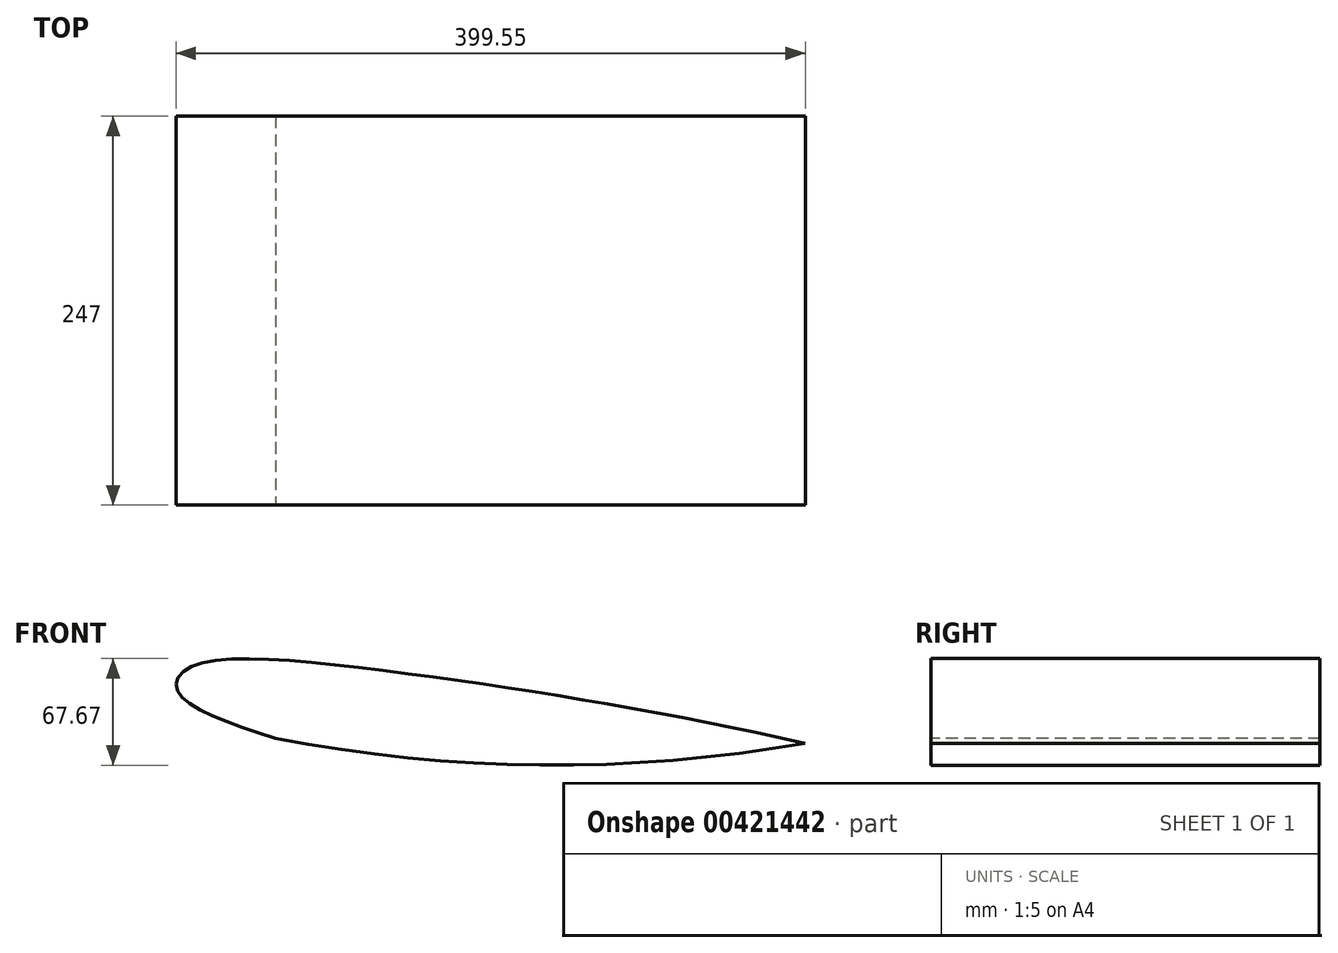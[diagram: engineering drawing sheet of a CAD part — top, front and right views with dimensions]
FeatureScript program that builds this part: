
annotation { "Feature Type Name" : "Feature", "Feature Type Description" : "" }
export const myFeature = defineFeature(function(context is Context, id is Id, definition is map)
    precondition{}
    {
        {
            var Q0;
            Q0=qCreatedBy(makeId("Front.planeOp"),FACE);
            var sketch = newSketch(context, id + "F0", { "sketchPlane" : qUnion([Q0])});
            skPoint(sketch, "E0", {"position": v(-1480.69, 132.06) * mm});
            skPoint(sketch, "E1", {"position": v(-1082.17, 99.2) * mm});
            skPoint(sketch, "E2", {"position": v(-1473.01, 147.53) * mm});
            skPoint(sketch, "E3", {"position": v(-1418.54, 102.28) * mm});
            skPoint(sketch, "E4", {"position": v(-1334.5, 143.28) * mm});
            skArc(sketch, "E5", {"start": v(-1418.54, 102.28) * mm, "mid": v(-1250.5, 85.26) * mm, "end": v(-1082.17, 99.2) * mm});
            skArc(sketch, "E6", {"start": v(-1334.5, 143.28) * mm, "mid": v(-1207.83, 124.11) * mm, "end": v(-1082.17, 99.2) * mm});
            skFitSpline(sketch, "E7", {"points": [v(-1418.54, 102.28) * mm, v(-1480.69, 132.06) * mm, v(-1473.01, 147.53) * mm, v(-1334.5, 143.28) * mm], "startDerivative": vector(-247.74, 81.4) * mm, "endDerivative": vector(361.63, -46.33) * mm});
            skSolve(sketch);
        }
        {
            var Q0;
            Q0=makeQuery(id+"F0.imprint","IMPRINT",FACE,{"disambiguationData":[TD([[makeQuery(id+"F0.imprint","IMPRINT",EDGE,{"derivedFrom":sQuery(id+"F0.wireOp",EDGE,"b7jMxSVx-ydCp-oYOB-XKka-a6bvCK3LPIrZ")}),1.0]])]});
            var Q1;
            Q1=makeQuery(id+"F0.imprint","IMPRINT",FACE,{"disambiguationData":[TD([[makeQuery(id+"F0.imprint","IMPRINT",EDGE,{"derivedFrom":sQuery(id+"F0.wireOp",EDGE,"E5")}),1.0]])]});
            extrude(context, id + "F1", {"entities" : qUnion([Q0, Q1]), "oppositeDirection" : true, "depth" : 247 * mm});
        }
    });
